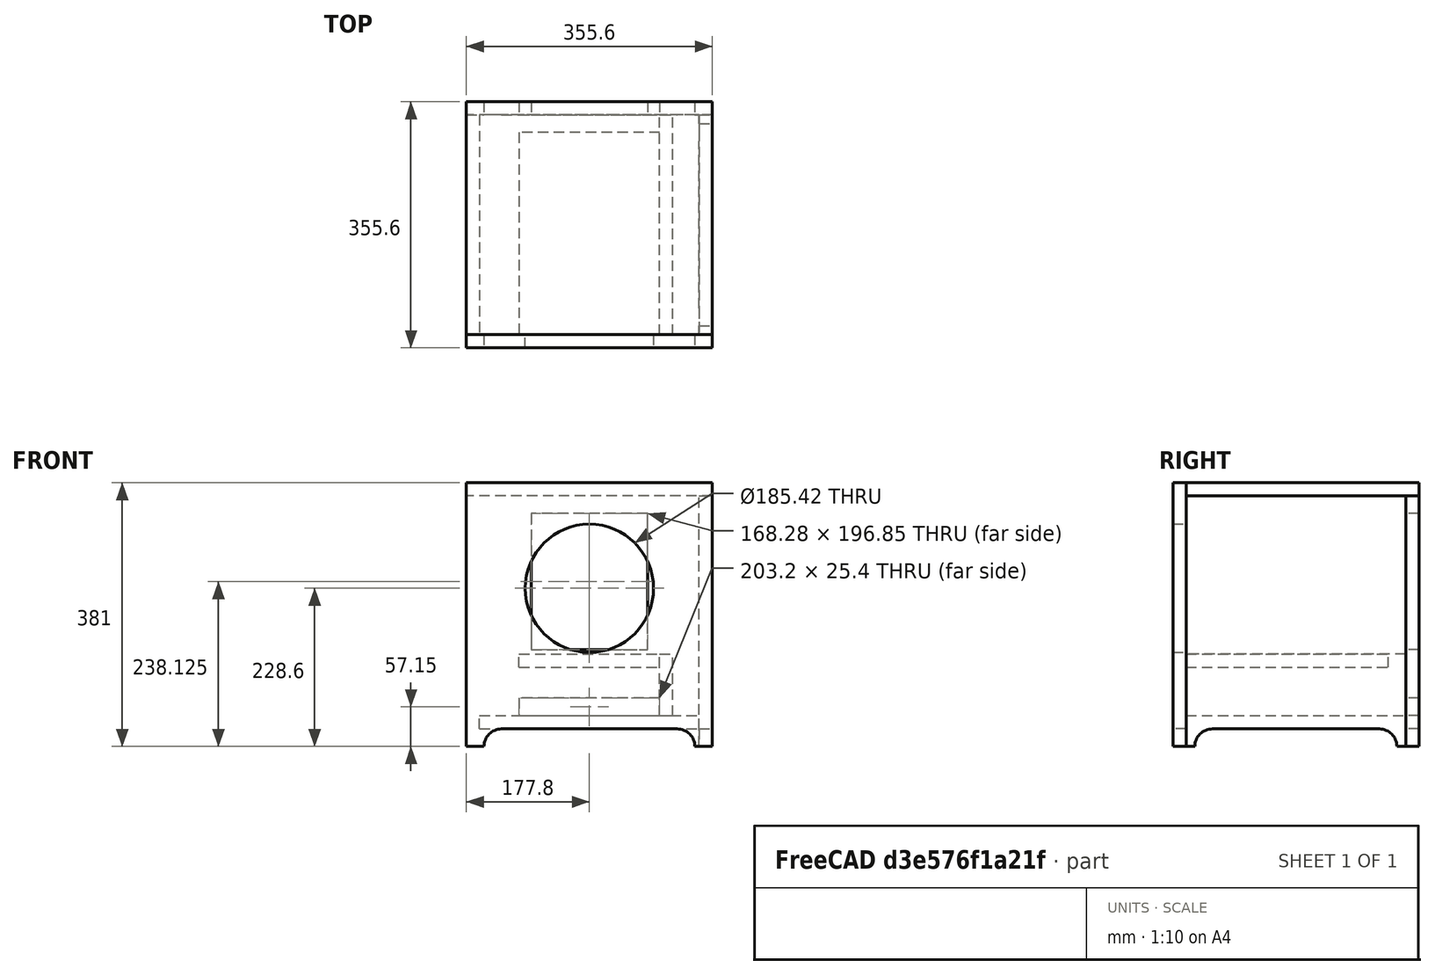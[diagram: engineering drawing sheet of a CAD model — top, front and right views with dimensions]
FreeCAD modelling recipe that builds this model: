
FCSTD DOCUMENT  (FreeCAD 1.0R39319 (Git))
Label: Turtle 2 Subwoofer
License: All rights reserved
objects: PartDesign::Body×10, Sketcher::SketchObject×7, PartDesign::Pad×7, PartDesign::FeatureBase×3, Assembly::JointGroup×1, Assembly::AssemblyObject×1
note: 51 computed .brp shape members not serialized (recipe doc carries the construction recipe); baked Part::Feature solids carry a one-line shape summary decoded from their .brp

FEATURE [Assembly::JointGroup] Joints
FEATURE [Sketcher::SketchObject] Sketch
  ArcFitTolerance = 1e-06
  AttachmentSupport = -> [XZ_Plane001]
  FullyConstrained = true
  MakeInternals = false
  MapMode = 5
  Placement = pos=(0,0,0) rot=(1,0,0;1.5708rad)
  sketch-geometry (17):
    g0: LineSegment [constr] StartX=0 StartY=0 StartZ=0 EndX=355.6 EndY=0 EndZ=0
    g1: LineSegment StartX=355.6 StartY=0 StartZ=0 EndX=355.6 EndY=381 EndZ=0
    g2: LineSegment StartX=355.6 StartY=381 StartZ=0 EndX=0 EndY=381 EndZ=0
    g3: LineSegment StartX=0 StartY=381 StartZ=0 EndX=0 EndY=0 EndZ=0
    g4: GeomPoint X=177.8 Y=0 Z=0
    g5: LineSegment [constr] StartX=177.8 StartY=0 StartZ=0 EndX=177.8 EndY=25.4 EndZ=0
    g6: LineSegment StartX=0 StartY=0 StartZ=0 EndX=25.4 EndY=3.1e-15 EndZ=0
    g7: LineSegment StartX=330.2 StartY=0 StartZ=0 EndX=355.6 EndY=0 EndZ=0
    g8: GeomPoint X=50.8 Y=0 Z=0
    g9: GeomPoint [constr] X=304.8 Y=0 Z=0
    g10: LineSegment [constr] StartX=0 StartY=25.4 StartZ=0 EndX=355.6 EndY=25.4 EndZ=0
    g11: LineSegment [constr] StartX=50.8 StartY=0 StartZ=0 EndX=50.8 EndY=25.4 EndZ=0
    g12: ArcOfCircle CenterX=50.8 CenterY=0 CenterZ=0 NormalX=0 NormalY=0 NormalZ=1 AngleXU=0 Radius=25.4 StartAngle=1.5708 EndAngle=3.14159
    g13: ArcOfCircle CenterX=304.8 CenterY=3.4e-15 CenterZ=0 NormalX=0 NormalY=0 NormalZ=1 AngleXU=0 Radius=25.4 StartAngle=0 EndAngle=1.5708
    g14: LineSegment StartX=50.8 StartY=25.4 StartZ=0 EndX=304.8 EndY=25.4 EndZ=0
    g15: LineSegment [constr] StartX=177.8 StartY=0 StartZ=0 EndX=177.8 EndY=381 EndZ=0
    g16: Circle CenterX=177.8 CenterY=228.6 CenterZ=0 NormalX=0 NormalY=0 NormalZ=1 AngleXU=0 Radius=92.71
  constraints (44):
    c: Coincident(g0,g1)
    c: Coincident(g1,g2)
    c: Coincident(g2,g3)
    c: Coincident(g3,g0)
    c: Horizontal(g0)
    c: Horizontal(g2)
    c: Vertical(g1)
    c: Vertical(g3)
    c: DistanceX(g2,g2) = 355.6
    c: DistanceY(g1,g1) = 381
    c: Coincident(g0,g-1)
    c: PointOnObject(g6,g0)
    c: Symmetric(g0,g0,g4)
    c: Coincident(g5,g4)
    c: Coincident(g6,g0)
    c: Coincident(g7,g0)
    c: Horizontal(g7)
    c: Symmetric(g6,g7,g5)
    c: DistanceX(g7,g7) = 25.4
    c: PointOnObject(g8,g0)
    c: DistanceX(g6,g8) = 25.4
    c: PointOnObject(g9,g0)
    c: DistanceX(g9,g7) = 25.4
    c: PointOnObject(g10,g3)
    c: PointOnObject(g10,g1)
    c: Horizontal(g10)
    c: Distance(g0,g10) = 25.4
    c: PointOnObject(g5,g10)
    c: Coincident(g11,g8)
    c: PointOnObject(g11,g10)
    c: Coincident(g12,g6)
    c: Coincident(g12,g11)
    c: Coincident(g8,g12)
    c: Equal(g12,g13)
    c: Symmetric(g12,g13,g5)
    c: Symmetric(g12,g13,g5)
    c: Coincident(g14,g11)
    c: Coincident(g14,g13)
    c: Coincident(g15,g4)
    c: Symmetric(g2,g2,g15)
    c: Diameter(g16) = 185.42
    c: PointOnObject(g16,g15)
    c: DistanceY(g16,g15) = 152.4
    c: DistanceY(g5,g16) = 203.2
FEATURE [PartDesign::Pad] Pad
  Direction = (0,-1,2e-16)
  Length = 19.05
  Length2 = 10
  Placement = pos=(0,0,0) rot=(1,0,0;1.5708rad)
  Profile = -> Sketch
  ReferenceAxis = -> Sketch [N_Axis]
  Suppressed = false
  Type = 0
FEATURE [PartDesign::Body] Body  label="Front"
  AllowCompound = false
  Group = -> [Sketch,Pad]
  Origin = -> Origin001
  Tip = -> Pad
FEATURE [Sketcher::SketchObject] Sketch001
  ArcFitTolerance = 1e-06
  AttachmentSupport = -> [XZ_Plane002]
  FullyConstrained = true
  MakeInternals = false
  MapMode = 5
  Placement = pos=(0,0,0) rot=(1,0,0;1.5708rad)
  sketch-geometry (28):
    g0: LineSegment [constr] StartX=0 StartY=0 StartZ=0 EndX=355.6 EndY=0 EndZ=0
    g1: LineSegment StartX=355.6 StartY=0 StartZ=0 EndX=355.6 EndY=361.95 EndZ=0
    g2: LineSegment StartX=355.6 StartY=361.95 StartZ=0 EndX=0 EndY=361.95 EndZ=0
    g3: LineSegment StartX=0 StartY=361.95 StartZ=0 EndX=0 EndY=0 EndZ=0
    g4: GeomPoint X=177.8 Y=0 Z=0
    g5: LineSegment [constr] StartX=177.8 StartY=0 StartZ=0 EndX=177.8 EndY=25.4 EndZ=0
    g6: LineSegment StartX=0 StartY=0 StartZ=0 EndX=25.4 EndY=3.1e-15 EndZ=0
    g7: LineSegment StartX=330.2 StartY=0 StartZ=0 EndX=355.6 EndY=0 EndZ=0
    g8: GeomPoint X=50.8 Y=0 Z=0
    g9: GeomPoint [constr] X=304.8 Y=0 Z=0
    g10: LineSegment [constr] StartX=0 StartY=25.4 StartZ=0 EndX=355.6 EndY=25.4 EndZ=0
    g11: LineSegment [constr] StartX=50.8 StartY=0 StartZ=0 EndX=50.8001 EndY=25.4 EndZ=0
    g12: ArcOfCircle CenterX=50.8 CenterY=0 CenterZ=0 NormalX=0 NormalY=0 NormalZ=1 AngleXU=0 Radius=25.4 StartAngle=1.57079 EndAngle=3.14159
    g13: ArcOfCircle CenterX=304.8 CenterY=1.3e-15 CenterZ=0 NormalX=0 NormalY=0 NormalZ=1 AngleXU=0 Radius=25.4 StartAngle=0 EndAngle=1.5708
    g14: LineSegment StartX=50.8001 StartY=25.4 StartZ=0 EndX=304.8 EndY=25.4 EndZ=0
    g15: LineSegment [constr] StartX=0 StartY=44.45 StartZ=0 EndX=355.6 EndY=44.45 EndZ=0
    g16: LineSegment [constr] StartX=0 StartY=69.85 StartZ=0 EndX=355.6 EndY=69.85 EndZ=0
    g17: LineSegment [constr] StartX=76.2 StartY=0 StartZ=0 EndX=76.2 EndY=69.85 EndZ=0
    g18: LineSegment StartX=76.2 StartY=69.85 StartZ=0 EndX=76.2 EndY=44.45 EndZ=0
    g19: LineSegment StartX=76.2 StartY=44.45 StartZ=0 EndX=279.4 EndY=44.45 EndZ=0
    g20: LineSegment StartX=279.4 StartY=44.45 StartZ=0 EndX=279.4 EndY=69.85 EndZ=0
    g21: LineSegment StartX=279.4 StartY=69.85 StartZ=0 EndX=76.2 EndY=69.85 EndZ=0
    g22: LineSegment [constr] StartX=177.8 StartY=0 StartZ=0 EndX=177.8 EndY=361.95 EndZ=0
    g23: LineSegment StartX=93.6625 StartY=139.7 StartZ=0 EndX=261.938 EndY=139.7 EndZ=0
    g24: LineSegment StartX=261.938 StartY=139.7 StartZ=0 EndX=261.938 EndY=336.55 EndZ=0
    g25: LineSegment StartX=261.938 StartY=336.55 StartZ=0 EndX=93.6625 EndY=336.55 EndZ=0
    g26: LineSegment StartX=93.6625 StartY=336.55 StartZ=0 EndX=93.6625 EndY=139.7 EndZ=0
    g27: GeomPoint X=177.8 Y=238.125 Z=0
  constraints (76):
    c: Coincident(g0,g1)
    c: Coincident(g1,g2)
    c: Coincident(g2,g3)
    c: Coincident(g3,g0)
    c: Horizontal(g0)
    c: Horizontal(g2)
    c: Vertical(g1)
    c: Vertical(g3)
    c: DistanceX(g2,g2) = 355.6
    c: DistanceY(g1,g1) = 361.95
    c: Coincident(g0,g-1)
    c: PointOnObject(g6,g0)
    c: Symmetric(g0,g0,g4)
    c: Coincident(g5,g4)
    c: Coincident(g6,g0)
    c: Coincident(g7,g0)
    c: Horizontal(g7)
    c: Symmetric(g6,g7,g5)
    c: DistanceX(g7,g7) = 25.4
    c: PointOnObject(g8,g0)
    c: DistanceX(g6,g8) = 25.4
    c: PointOnObject(g9,g0)
    c: DistanceX(g9,g7) = 25.4
    c: PointOnObject(g10,g3)
    c: PointOnObject(g10,g1)
    c: Horizontal(g10)
    c: Distance(g0,g10) = 25.4
    c: PointOnObject(g5,g10)
    c: Coincident(g11,g8)
    c: PointOnObject(g11,g10)
    c: Coincident(g12,g6)
    c: Coincident(g12,g11)
    c: Coincident(g8,g12)
    c: Equal(g12,g13)
    c: Symmetric(g12,g13,g5)
    c: Symmetric(g12,g13,g5)
    c: Coincident(g14,g11)
    c: Coincident(g14,g13)
    c: PointOnObject(g15,g3)
    c: PointOnObject(g15,g1)
    c: Horizontal(g15)
    c: Distance(g15,g14) = 19.05
    c: PointOnObject(g16,g3)
    c: PointOnObject(g16,g1)
    c: Horizontal(g16)
    c: Distance(g15,g16) = 25.4
    c: PointOnObject(g17,g0)
    c: PointOnObject(g17,g16)
    c: Vertical(g17)
    c: Distance(g3,g17) = 76.2
    c: Coincident(g18,g19)
    c: Coincident(g19,g20)
    c: Coincident(g20,g21)
    c: Coincident(g21,g18)
    c: Vertical(g18)
    c: Vertical(g20)
    c: Horizontal(g19)
    c: Horizontal(g21)
    c: Coincident(g18,g17)
    c: PointOnObject(g19,g15)
    c: DistanceX(g21,g21) = 203.2
    c: Coincident(g22,g4)
    c: Symmetric(g2,g2,g22)
    c: Coincident(g23,g24)
    c: Coincident(g24,g25)
    c: Coincident(g25,g26)
    c: Coincident(g26,g23)
    c: Horizontal(g23)
    c: Horizontal(g25)
    c: Vertical(g24)
    c: Vertical(g26)
    c: Symmetric(g25,g23,g27)
    c: Distance(g24,g26) = 168.275
    c: Distance(g23,g25) = 196.85
    c: PointOnObject(g27,g22)
    c: Distance(g2,g25) = 25.4
FEATURE [PartDesign::Pad] Pad001
  Direction = (0,-1,2e-16)
  Length = 19.05
  Length2 = 10
  Placement = pos=(0,0,0) rot=(1,0,0;1.5708rad)
  Profile = -> Sketch001
  ReferenceAxis = -> Sketch001 [N_Axis]
  Suppressed = false
  Type = 0
FEATURE [PartDesign::Body] Body001  label="Rear"
  AllowCompound = false
  Group = -> [Sketch001,Pad001]
  Origin = -> Origin002
  Placement = pos=(0,336.55,0) rot=(0,0,1;0rad)
  Tip = -> Pad001
FEATURE [Sketcher::SketchObject] Sketch002
  ArcFitTolerance = 1e-06
  AttachmentSupport = -> [XZ_Plane003]
  FullyConstrained = true
  MakeInternals = false
  MapMode = 5
  Placement = pos=(0,0,0) rot=(1,0,0;1.5708rad)
  sketch-geometry (15):
    g0: LineSegment [constr] StartX=0 StartY=0 StartZ=0 EndX=317.5 EndY=0 EndZ=0
    g1: LineSegment StartX=317.5 StartY=0 StartZ=0 EndX=317.5 EndY=361.95 EndZ=0
    g2: LineSegment StartX=317.5 StartY=361.95 StartZ=0 EndX=0 EndY=361.95 EndZ=0
    g3: LineSegment StartX=0 StartY=361.95 StartZ=0 EndX=0 EndY=0 EndZ=0
    g4: GeomPoint X=158.75 Y=0 Z=0
    g5: LineSegment [constr] StartX=158.75 StartY=0 StartZ=0 EndX=158.75 EndY=25.4 EndZ=0
    g6: LineSegment StartX=0 StartY=0 StartZ=0 EndX=12.7 EndY=3.1e-15 EndZ=0
    g7: LineSegment StartX=304.8 StartY=0 StartZ=0 EndX=317.5 EndY=0 EndZ=0
    g8: GeomPoint X=38.1 Y=0 Z=0
    g9: GeomPoint [constr] X=279.4 Y=0 Z=0
    g10: LineSegment [constr] StartX=0 StartY=25.4 StartZ=0 EndX=317.5 EndY=25.4 EndZ=0
    g11: LineSegment [constr] StartX=38.1 StartY=0 StartZ=0 EndX=38.0999 EndY=25.4 EndZ=0
    g12: ArcOfCircle CenterX=38.1 CenterY=0 CenterZ=0 NormalX=0 NormalY=0 NormalZ=1 AngleXU=0 Radius=25.4 StartAngle=1.5708 EndAngle=3.14159
    g13: ArcOfCircle CenterX=279.4 CenterY=-4e-16 CenterZ=0 NormalX=0 NormalY=0 NormalZ=1 AngleXU=0 Radius=25.4 StartAngle=0 EndAngle=1.57079
    g14: LineSegment StartX=38.0999 StartY=25.4 StartZ=0 EndX=279.4 EndY=25.4 EndZ=0
  constraints (38):
    c: Coincident(g0,g1)
    c: Coincident(g1,g2)
    c: Coincident(g2,g3)
    c: Coincident(g3,g0)
    c: Horizontal(g0)
    c: Horizontal(g2)
    c: Vertical(g1)
    c: Vertical(g3)
    c: DistanceX(g2,g2) = 317.5
    c: DistanceY(g1,g1) = 361.95
    c: Coincident(g0,g-1)
    c: PointOnObject(g6,g0)
    c: Symmetric(g0,g0,g4)
    c: Coincident(g5,g4)
    c: Coincident(g6,g0)
    c: Coincident(g7,g0)
    c: Horizontal(g7)
    c: Symmetric(g6,g7,g5)
    c: DistanceX(g7,g7) = 12.7
    c: PointOnObject(g8,g0)
    c: DistanceX(g6,g8) = 25.4
    c: PointOnObject(g9,g0)
    c: DistanceX(g9,g7) = 25.4
    c: PointOnObject(g10,g3)
    c: PointOnObject(g10,g1)
    c: Horizontal(g10)
    c: Distance(g0,g10) = 25.4
    c: PointOnObject(g5,g10)
    c: Coincident(g11,g8)
    c: PointOnObject(g11,g10)
    c: Coincident(g12,g6)
    c: Coincident(g12,g11)
    c: Coincident(g8,g12)
    c: Equal(g12,g13)
    c: Symmetric(g12,g13,g5)
    c: Symmetric(g12,g13,g5)
    c: Coincident(g14,g11)
    c: Coincident(g14,g13)
FEATURE [PartDesign::Pad] Pad002
  Direction = (0,-1,2e-16)
  Length = 19.05
  Length2 = 10
  Placement = pos=(0,0,0) rot=(1,0,0;1.5708rad)
  Profile = -> Sketch002
  ReferenceAxis = -> Sketch002 [N_Axis]
  Suppressed = false
  Type = 0
FEATURE [PartDesign::Body] Body002  label="left"
  AllowCompound = false
  Group = -> [Sketch002,Pad002]
  Origin = -> Origin003
  Placement = pos=(0,0,0) rot=(0,0,1;1.5708rad)
  Tip = -> Pad002
FEATURE [PartDesign::FeatureBase] Clone
  BaseFeature = -> Body002
  Placement = pos=(0,0,0) rot=(0,0,1;1.5708rad)
  Suppressed = false
FEATURE [PartDesign::Body] Body003  label="right"
  AllowCompound = false
  Group = -> [Clone]
  Origin = -> Origin004
  Placement = pos=(336.55,0,0) rot=(0,0,1;0rad)
  Tip = -> Clone
FEATURE [Sketcher::SketchObject] Sketch003
  ArcFitTolerance = 1e-06
  AttachmentSupport = -> [XY_Plane005]
  FullyConstrained = true
  MakeInternals = false
  MapMode = 5
  sketch-geometry (4):
    g0: LineSegment StartX=0 StartY=0 StartZ=0 EndX=355.6 EndY=0 EndZ=0
    g1: LineSegment StartX=355.6 StartY=0 StartZ=0 EndX=355.6 EndY=336.55 EndZ=0
    g2: LineSegment StartX=355.6 StartY=336.55 StartZ=0 EndX=0 EndY=336.55 EndZ=0
    g3: LineSegment StartX=0 StartY=336.55 StartZ=0 EndX=0 EndY=0 EndZ=0
  constraints (11):
    c: Coincident(g0,g1)
    c: Coincident(g1,g2)
    c: Coincident(g2,g3)
    c: Coincident(g3,g0)
    c: Horizontal(g0)
    c: Horizontal(g2)
    c: Vertical(g1)
    c: Vertical(g3)
    c: Coincident(g0,g-1)
    c: DistanceX(g2,g2) = 355.6
    c: DistanceY(g3,g3) = 336.55
FEATURE [PartDesign::Pad] Pad003
  Direction = (0,0,1)
  Length = 19.05
  Length2 = 10
  Profile = -> Sketch003
  ReferenceAxis = -> Sketch003 [N_Axis]
  Suppressed = false
  Type = 0
FEATURE [PartDesign::Body] Body004  label="top"
  AllowCompound = false
  Group = -> [Sketch003,Pad003]
  Origin = -> Origin005
  Placement = pos=(0,0,361.95) rot=(0,0,1;0rad)
  Tip = -> Pad003
FEATURE [Sketcher::SketchObject] Sketch004
  ArcFitTolerance = 1e-06
  AttachmentSupport = -> [XY_Plane006]
  FullyConstrained = true
  MakeInternals = false
  MapMode = 5
  sketch-geometry (4):
    g0: LineSegment StartX=0 StartY=0 StartZ=0 EndX=317.5 EndY=0 EndZ=0
    g1: LineSegment StartX=317.5 StartY=0 StartZ=0 EndX=317.5 EndY=317.5 EndZ=0
    g2: LineSegment StartX=317.5 StartY=317.5 StartZ=0 EndX=0 EndY=317.5 EndZ=0
    g3: LineSegment StartX=0 StartY=317.5 StartZ=0 EndX=0 EndY=0 EndZ=0
  constraints (11):
    c: Coincident(g0,g1)
    c: Coincident(g1,g2)
    c: Coincident(g2,g3)
    c: Coincident(g3,g0)
    c: Horizontal(g0)
    c: Horizontal(g2)
    c: Vertical(g1)
    c: Vertical(g3)
    c: DistanceX(g2,g2) = 317.5
    c: DistanceY(g1,g1) = 317.5
    c: Coincident(g-1,g0)
FEATURE [PartDesign::Pad] Pad004
  Direction = (0,0,1)
  Length = 19.05
  Length2 = 10
  Profile = -> Sketch004
  ReferenceAxis = -> Sketch004 [N_Axis]
  Suppressed = false
  Type = 0
FEATURE [PartDesign::Body] Body005  label="bottom"
  AllowCompound = false
  Group = -> [Sketch004,Pad004]
  Origin = -> Origin006
  Placement = pos=(19.05,0,25.4) rot=(0,0,1;0rad)
  Tip = -> Pad004
FEATURE [Sketcher::SketchObject] Sketch005
  ArcFitTolerance = 1e-06
  AttachmentSupport = -> [XY_Plane007]
  FullyConstrained = true
  MakeInternals = false
  MapMode = 5
  sketch-geometry (4):
    g0: LineSegment StartX=0 StartY=0 StartZ=0 EndX=203.2 EndY=0 EndZ=0
    g1: LineSegment StartX=203.2 StartY=0 StartZ=0 EndX=203.2 EndY=292.1 EndZ=0
    g2: LineSegment StartX=203.2 StartY=292.1 StartZ=0 EndX=0 EndY=292.1 EndZ=0
    g3: LineSegment StartX=0 StartY=292.1 StartZ=0 EndX=0 EndY=0 EndZ=0
  constraints (11):
    c: Coincident(g0,g1)
    c: Coincident(g1,g2)
    c: Coincident(g2,g3)
    c: Coincident(g3,g0)
    c: Horizontal(g0)
    c: Horizontal(g2)
    c: Vertical(g1)
    c: Vertical(g3)
    c: Coincident(g0,g-1)
    c: DistanceX(g2,g2) = 203.2
    c: DistanceY(g1,g1) = 292.1
FEATURE [PartDesign::Pad] Pad005
  Direction = (0,0,1)
  Length = 19.05
  Length2 = 10
  Profile = -> Sketch005
  ReferenceAxis = -> Sketch005 [N_Axis]
  Suppressed = false
  Type = 0
FEATURE [PartDesign::Body] Body006  label="port-mid"
  AllowCompound = false
  Group = -> [Sketch005,Pad005]
  Origin = -> Origin007
  Placement = pos=(76.2,25.4,69.85) rot=(0,0,1;0rad)
  Tip = -> Pad005
FEATURE [PartDesign::FeatureBase] Clone001
  BaseFeature = -> Body006
  Placement = pos=(76.2,25.4,69.85) rot=(0,0,1;0rad)
  Suppressed = false
FEATURE [PartDesign::Body] Body007  label="port-top"
  AllowCompound = false
  Group = -> [Clone001]
  Origin = -> Origin008
  Placement = pos=(0,-25.4,44.45) rot=(0,0,1;0rad)
  Tip = -> Clone001
FEATURE [Sketcher::SketchObject] Sketch006
  ArcFitTolerance = 1e-06
  AttachmentSupport = -> [YZ_Plane009]
  FullyConstrained = true
  MakeInternals = false
  MapMode = 5
  Placement = pos=(0,0,0) rot=(0.57735,0.57735,0.57735;2.0944rad)
  sketch-geometry (4):
    g0: LineSegment StartX=0 StartY=0 StartZ=0 EndX=317.5 EndY=0 EndZ=0
    g1: LineSegment StartX=317.5 StartY=0 StartZ=0 EndX=317.5 EndY=88.9 EndZ=0
    g2: LineSegment StartX=317.5 StartY=88.9 StartZ=0 EndX=0 EndY=88.9 EndZ=0
    g3: LineSegment StartX=0 StartY=88.9 StartZ=0 EndX=0 EndY=0 EndZ=0
  constraints (11):
    c: Coincident(g0,g1)
    c: Coincident(g1,g2)
    c: Coincident(g2,g3)
    c: Coincident(g3,g0)
    c: Horizontal(g0)
    c: Horizontal(g2)
    c: Vertical(g1)
    c: Vertical(g3)
    c: Distance(g1,g3) = 317.5
    c: Distance(g0,g2) = 88.9
    c: Coincident(g0,g-1)
FEATURE [PartDesign::Pad] Pad006
  Direction = (1,0,0)
  Length = 19.05
  Length2 = 10
  Placement = pos=(0,0,0) rot=(1,1,1;2.0944rad)
  Profile = -> Sketch006
  ReferenceAxis = -> Sketch006 [N_Axis]
  Suppressed = false
  Type = 0
FEATURE [PartDesign::Body] Body008  label="port-left"
  AllowCompound = false
  Group = -> [Sketch006,Pad006]
  Origin = -> Origin009
  Placement = pos=(57.15,0,44.45) rot=(0,0,1;0rad)
  Tip = -> Pad006
FEATURE [PartDesign::FeatureBase] Clone002
  BaseFeature = -> Body008
  Placement = pos=(57.15,0,44.45) rot=(0,0,1;0rad)
  Suppressed = false
FEATURE [PartDesign::Body] Body009  label="port-right"
  AllowCompound = false
  Group = -> [Clone002]
  Origin = -> Origin010
  Placement = pos=(222.25,0,0) rot=(0,0,1;0rad)
  Tip = -> Clone002
FEATURE [Assembly::AssemblyObject] Assembly
  Group = -> [Joints,Body,Body001,Body002,Body003,Body004,Body005,Body006,Body007,Body008,Body009]
  Origin = -> Origin
  Type = Assembly
